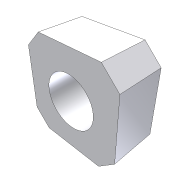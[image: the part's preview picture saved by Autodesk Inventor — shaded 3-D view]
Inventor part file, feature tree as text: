
AUTODESK INVENTOR PART (.ipt)
format: ipt  version: unknown  size: 169,472 bytes
history: native  units: in
note: dims shown in document units (in); Inventor stores cm internally (conversion verified against a paired STEP export)
features: extrude x1, chamfer x1, sketch x1
ambient origin geometry x8: Origin, YZ Plane, XZ Plane, XY Plane, X Axis, Y Axis, Z Axis, Center Point
feature tree (3):
  extrude  "Extrusion7"  Depth=0.6299in
  chamfer  "Chamfer2"  Distance=1.1811in
  sketch  "Sketch7"  dims[d21=0.7874in d33=0.6299in d34=1.1811in d35=0.5512in d36=0.0in d37=0.1969in d38=0.0787in d39=45.0deg]
